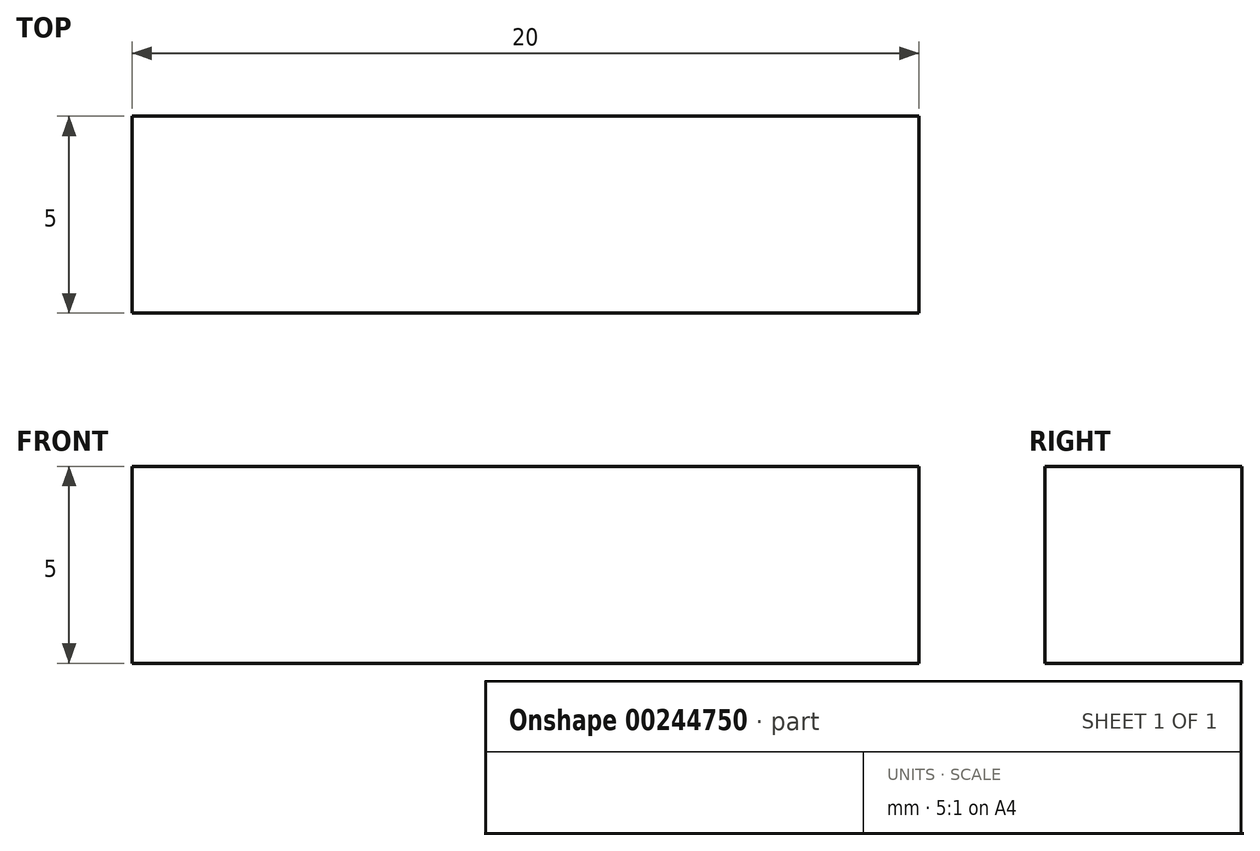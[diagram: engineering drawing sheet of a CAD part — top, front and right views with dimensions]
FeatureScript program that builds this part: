
annotation { "Feature Type Name" : "Feature", "Feature Type Description" : "" }
export const myFeature = defineFeature(function(context is Context, id is Id, definition is map)
    precondition{}
    {
        {
            var Q0;
            Q0=qCreatedBy(makeId("Top.planeOp"),FACE);
            var sketch = newSketch(context, id + "F0", { "sketchPlane" : qUnion([Q0])});
            skLineSegment(sketch, "E0.bottom", {"start": v(10, 2.5) * mm, "end": v(-10, 2.5) * mm});
            skLineSegment(sketch, "E0.top", {"start": v(10, -2.5) * mm, "end": v(-10, -2.5) * mm});
            skLineSegment(sketch, "E0.left", {"start": v(10, 2.5) * mm, "end": v(10, -2.5) * mm});
            skLineSegment(sketch, "E0.right", {"start": v(-10, 2.5) * mm, "end": v(-10, -2.5) * mm});
            skPoint(sketch, "E0.middle", {"position": v(0, 0) * mm});
            skSolve(sketch);
        }
        {
            var Q0;
            Q0 = qSketchRegion(id + "F0", true);
            extrude(context, id + "F1", {"entities" : qUnion([Q0]), "depth" : 5 * mm});
        }
    });
